# Revit family: Červinka_Přenosný hasicí přístroj_Pro hašení požárů lithiových baterií LITH EX9
name_source: partatom
category: Speciální vybavení
units: mm (PartAtom-declared; Revit-internal decimal feet)

## family parameters
Bod výpočtu místnosti = Ne
Kóta kulaté spojky = Použít průměr
Ořezat dutým tvarem při načtení = Ne
Sdílené = Ne
Typ dílu = Normální
Vždy vertikální = Ano
Založené na pracovní rovině = Ano

## types (1)
- LITH EX9
    Cena = 0 $
    Hasicí schopnost_ = 13A
    Hasivo = AVD
    Hmotnost = 15.20 kg
    Hmotnost hasiva = 9.00 kg
    Komentáře k typům = Přenosný hasicí přístroj na požáry lithiových baterií
    Kód sestavy = PZ.
    Kód_ = 0271
    Materiál hadice = Černá
    Materiál podstavce = Zelená
    Maximální teplota použití = 50 °C
    Minimální teplota použití = 5 °C
    Model = LITH EX9
    Objem lahve = 11.33 L
    Popis = Přenosný hasicí přístroj
    Povrchová úprava lahve = Červená
    Pracovní tlak = 15.0 bar
    Průměr lahve = 170 mm  [stored 0.557743 ft]
    Splnění norem = EN3
    Typ zařízení_ = LITH EX9
    Třída požáru A = Ano
    Třída požáru B = Ne
    Třída požáru C = Ne
    Třída požáru D = Ne
    Třída požáru F = Ne
    URL = http://www.hasicitechnika.com
    Výchozí výška = 1500 mm  [stored 4.92126 ft]
    Výrobce = ČERVINKA - CZECH REPUBLIC s.r.o.
    Výška k ventilu = 585 mm  [stored 1.91929 ft]
    Výška_ = 680 mm  [stored 2.23097 ft]
    Šířka_ = 195 mm  [stored 0.639764 ft]

note: [stored X ft] marks values corroborated as IEEE doubles in the binary element streams (Revit-internal decimal feet)
